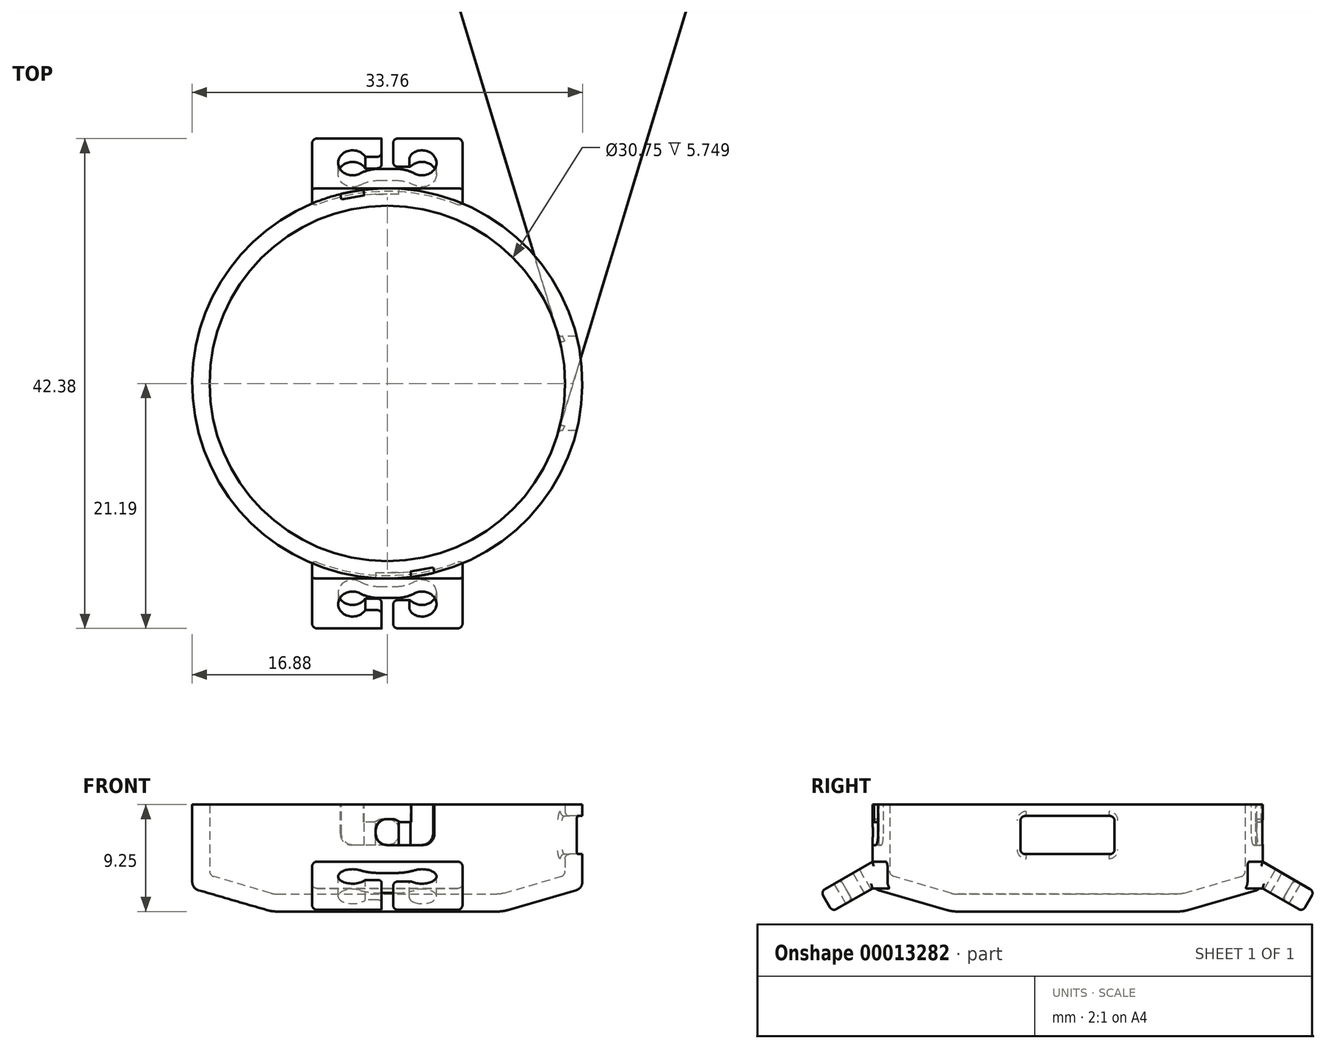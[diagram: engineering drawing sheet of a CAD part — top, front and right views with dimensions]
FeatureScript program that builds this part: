
annotation { "Feature Type Name" : "Feature", "Feature Type Description" : "" }
export const myFeature = defineFeature(function(context is Context, id is Id, definition is map)
    precondition{}
    {
        {
            var Q0;
            Q0=qCreatedBy(makeId("Front.planeOp"),FACE);
            var sketch = newSketch(context, id + "F0", { "sketchPlane" : qUnion([Q0])});
            skLineSegment(sketch, "E0", {"start": v(-16.88, 7.25) * mm, "end": v(-16.88, 0.56) * mm});
            skLineSegment(sketch, "E1", {"start": v(-16.33, -0.16) * mm, "end": v(-10.41, -1.88) * mm});
            skLineSegment(sketch, "E2", {"start": v(-9.57, -2) * mm, "end": v(0, -2) * mm});
            skLineSegment(sketch, "E3", {"start": v(0, -2) * mm, "end": v(0, -0.5) * mm});
            skLineSegment(sketch, "E4", {"start": v(0, -0.5) * mm, "end": v(-9.5, -0.5) * mm});
            skLineSegment(sketch, "E5", {"start": v(-10.06, -0.42) * mm, "end": v(-15.01, 1.02) * mm});
            skLineSegment(sketch, "E6", {"start": v(-15.38, 7.25) * mm, "end": v(-16.88, 7.25) * mm});
            skLineSegment(sketch, "E7", {"start": v(-15.38, 7.25) * mm, "end": v(-15.38, 1.5) * mm});
            skPoint(sketch, "E8.visualSharp", {"position": v(-16.88, 0) * mm});
            skArc(sketch, "E8.filletArc", {"start": v(-16.88, 0.56) * mm, "mid": v(-16.72, 0.11) * mm, "end": v(-16.33, -0.16) * mm});
            skPoint(sketch, "E9.visualSharp", {"position": v(-10, -2) * mm});
            skArc(sketch, "E9.filletArc", {"start": v(-10.41, -1.88) * mm, "mid": v(-10, -1.97) * mm, "end": v(-9.57, -2) * mm});
            skPoint(sketch, "E10.visualSharp", {"position": v(-15.38, 1.13) * mm});
            skArc(sketch, "E10.filletArc", {"start": v(-15.38, 1.5) * mm, "mid": v(-15.27, 1.2) * mm, "end": v(-15.01, 1.02) * mm});
            skPoint(sketch, "E11.visualSharp", {"position": v(-9.79, -0.5) * mm});
            skArc(sketch, "E11.filletArc", {"start": v(-10.06, -0.42) * mm, "mid": v(-9.78, -0.48) * mm, "end": v(-9.5, -0.5) * mm});
            skSolve(sketch);
        }
        {
            var Q0;
            Q0=makeQuery(id+"F0.imprint","IMPRINT",FACE,{"disambiguationData":[TD([[makeQuery(id+"F0.imprint","IMPRINT",EDGE,{"derivedFrom":sQuery(id+"F0.wireOp",EDGE,"E0")}),1.0]])]});
            var Q1;
            Q1=sQuery(id+"F0.wireOp",EDGE,"E3");
            revolve(context, id + "F1", {"entities" : qUnion([Q0]), "axis" : qUnion([Q1]), "revolveType" : RevolveType.FULL});
        }
        {
            var Q0;
            Q0=qCreatedBy(makeId("Right.planeOp"),FACE);
            var sketch = newSketch(context, id + "F2", { "sketchPlane" : qUnion([Q0])});
            skLineSegment(sketch, "E12", {"start": v(-15.38, 0) * mm, "end": v(-15.38, 2.3) * mm});
            skLineSegment(sketch, "E13", {"start": v(-15.38, 2.3) * mm, "end": v(-16.88, 2.3) * mm});
            skLineSegment(sketch, "E14", {"start": v(-16.88, 2.3) * mm, "end": v(-21.34, -0.27) * mm});
            skLineSegment(sketch, "E15", {"start": v(-21.34, -0.27) * mm, "end": v(-20.34, -2) * mm});
            skLineSegment(sketch, "E16", {"start": v(-20.34, -2) * mm, "end": v(-16.88, 0) * mm});
            skLineSegment(sketch, "E17", {"start": v(-16.88, 0) * mm, "end": v(-15.38, 0) * mm});
            skSolve(sketch);
        }
        {
            var Q0;
            Q0=makeQuery(id+"F2.imprint","IMPRINT",FACE,{"disambiguationData":[TD([[makeQuery(id+"F2.imprint","IMPRINT",EDGE,{"derivedFrom":sQuery(id+"F2.wireOp",EDGE,"E12")}),1.0]])]});
            extrude(context, id + "F3", {"entities" : qUnion([Q0]), "operationType" : NewBodyOperationType.ADD, "depth" : 6.5 * mm, "hasSecondDirection" : true, "secondDirectionOppositeDirection" : true, "secondDirectionDepth" : 6.5 * mm});
        }
        {
            var Q0;
            Q0=makeQuery(id+"F3.opExtrude","SWEPT_FACE",FACE,{"disambiguationData":[OSD([sQuery(id+"F2.wireOp",EDGE,"E14")])]});
            var sketch = newSketch(context, id + "F4", { "sketchPlane" : qUnion([Q0])});
            skLineSegment(sketch, "E18", {"start": v(-0.5, -18.61) * mm, "end": v(0.5, -18.61) * mm});
            skLineSegment(sketch, "E19", {"start": v(0.5, -18.61) * mm, "end": v(0.5, -16.61) * mm});
            skLineSegment(sketch, "E20", {"start": v(0.5, -16.61) * mm, "end": v(3, -16.61) * mm});
            skLineSegment(sketch, "E21", {"start": v(3, -16.61) * mm, "end": v(3, -15.41) * mm});
            skLineSegment(sketch, "E22", {"start": v(3, -15.41) * mm, "end": v(-3, -15.41) * mm});
            skLineSegment(sketch, "E23", {"start": v(-3, -15.41) * mm, "end": v(-3, -16.61) * mm});
            skLineSegment(sketch, "E24", {"start": v(-3, -16.61) * mm, "end": v(-0.5, -16.61) * mm});
            skLineSegment(sketch, "E25", {"start": v(-0.5, -16.61) * mm, "end": v(-0.5, -18.61) * mm});
            skCircle(sketch, "E26", {"center": v(-3, -16.01) * mm, "radius": 1.25 * mm});
            skCircle(sketch, "E27", {"center": v(3, -16.01) * mm, "radius": 1.25 * mm});
            skSolve(sketch);
        }
        {
            var Q0;
            {var subQ5=sQuery(id+"F4.wireOp",EDGE,"E23");Q0=makeQuery(id+"F4.imprint","IMPRINT",FACE,{"disambiguationData":[TD([[makeQuery(id+"F4.imprint","IMPRINT",EDGE,{"derivedFrom":subQ5}),-1.0]])]});}
            var Q1;
            {var subQ5=sQuery(id+"F4.wireOp",EDGE,"E23");Q1=makeQuery(id+"F4.imprint","IMPRINT",FACE,{"disambiguationData":[TD([[makeQuery(id+"F4.imprint","IMPRINT",EDGE,{"derivedFrom":subQ5}),1.0]])]});}
            var Q2;
            Q2=makeQuery(id+"F4.imprint","IMPRINT",FACE,{"disambiguationData":[TD([[makeQuery(id+"F4.imprint","IMPRINT",EDGE,{"derivedFrom":sQuery(id+"F4.wireOp",EDGE,"E18")}),-1.0]])]});
            var Q3;
            {var subQ5=sQuery(id+"F4.wireOp",EDGE,"E21");Q3=makeQuery(id+"F4.imprint","IMPRINT",FACE,{"disambiguationData":[TD([[makeQuery(id+"F4.imprint","IMPRINT",EDGE,{"derivedFrom":subQ5}),1.0]])]});}
            var Q4;
            {var subQ5=sQuery(id+"F4.wireOp",EDGE,"E21");Q4=makeQuery(id+"F4.imprint","IMPRINT",FACE,{"disambiguationData":[TD([[makeQuery(id+"F4.imprint","IMPRINT",EDGE,{"derivedFrom":subQ5}),-1.0]])]});}
            extrude(context, id + "F5", {"entities" : qUnion([Q0, Q1, Q2, Q3, Q4]), "operationType" : NewBodyOperationType.REMOVE, "endBound" : BoundingType.UP_TO_NEXT, "oppositeDirection" : true, "depth" : 25 * mm});
        }
        {
            var Q0;
            Q0=makeQuery(id+"F5.boolean.opBoolean","COPY",EDGE,{"derivedFrom":makeQuery(id+"F5.opExtrude","SWEPT_EDGE",EDGE,{"disambiguationData":[OSD([sQuery(id+"F4.wireOp",EDGE,"E22"),sQuery(id+"F4.wireOp",EDGE,"E26")])]})});
            var Q1;
            Q1=makeQuery(id+"F5.boolean.opBoolean","COPY",EDGE,{"derivedFrom":makeQuery(id+"F5.opExtrude","SWEPT_EDGE",EDGE,{"disambiguationData":[OSD([sQuery(id+"F4.wireOp",EDGE,"E22"),sQuery(id+"F4.wireOp",EDGE,"E27")])]})});
            fillet(context, id + "F6", {"entities" : qUnion([Q0, Q1]), "radius" : 3 * mm, "tangentPropagation" : true, "allowEdgeOverflow" : false});
        }
        {
            var Q0;
            Q0=makeQuery(id+"F5.boolean.opBoolean","COPY",EDGE,{"derivedFrom":makeQuery(id+"F5.opExtrude","SWEPT_EDGE",EDGE,{"disambiguationData":[OSD([sQuery(id+"F2.wireOp",EDGE,"E14"),sQuery(id+"F2.wireOp",EDGE,"E15"),sQuery(id+"F4.wireOp",EDGE,"E18"),sQuery(id+"F4.wireOp",EDGE,"E25")])]})});
            var Q1;
            Q1=makeQuery(id+"F5.boolean.opBoolean","COPY",EDGE,{"derivedFrom":makeQuery(id+"F5.opExtrude","SWEPT_EDGE",EDGE,{"disambiguationData":[OSD([sQuery(id+"F2.wireOp",EDGE,"E14"),sQuery(id+"F2.wireOp",EDGE,"E15"),sQuery(id+"F4.wireOp",EDGE,"E18"),sQuery(id+"F4.wireOp",EDGE,"E19")])]})});
            var Q2;
            Q2=makeQuery(id+"F5.boolean.opBoolean","COPY",EDGE,{"derivedFrom":makeQuery(id+"F5.opExtrude","SWEPT_EDGE",EDGE,{"disambiguationData":[OSD([sQuery(id+"F4.wireOp",EDGE,"E24"),sQuery(id+"F4.wireOp",EDGE,"E25")])]})});
            var Q3;
            Q3=makeQuery(id+"F5.boolean.opBoolean","COPY",EDGE,{"derivedFrom":makeQuery(id+"F5.opExtrude","SWEPT_EDGE",EDGE,{"disambiguationData":[OSD([sQuery(id+"F4.wireOp",EDGE,"E19"),sQuery(id+"F4.wireOp",EDGE,"E20")])]})});
            fillet(context, id + "F7", {"entities" : qUnion([Q0, Q1, Q2, Q3]), "radius" : .4 * mm, "tangentPropagation" : true, "allowEdgeOverflow" : false});
        }
        {
            var Q0;
            Q0=makeQuery(id+"F3.opExtrude","CAP_EDGE",EDGE,{"disambiguationData":[OSD([sQuery(id+"F2.wireOp",EDGE,"E13")])],"isStart":true});
            var Q1;
            Q1=makeQuery(id+"F3.opExtrude","CAP_EDGE",EDGE,{"disambiguationData":[OSD([sQuery(id+"F2.wireOp",EDGE,"E14")])],"isStart":true});
            var Q2;
            {var subQ0=sQuery(id+"F2.wireOp",EDGE,"E15");var subQ1=sQuery(id+"F2.wireOp",EDGE,"E14");Q2=makeQuery(id+"F5.boolean.opBoolean","SPLIT",EDGE,{"disambiguationData":[TD([makeQuery(id+"F5.opExtrude","SWEPT_FACE",FACE,{"disambiguationData":[OSD([sQuery(id+"F4.wireOp",EDGE,"E25")])]})])],"derivedFrom":makeQuery(id+"F3.opExtrude","SWEPT_EDGE",EDGE,{"disambiguationData":[OSD([subQ1,subQ0])]})});}
            var Q3;
            Q3=makeQuery(id+"F5.boolean.opBoolean","COPY",EDGE,{"derivedFrom":makeQuery(id+"F5.opExtrude","CAP_EDGE",EDGE,{"disambiguationData":[OSD([sQuery(id+"F4.wireOp",EDGE,"E26")])],"isStart":true})});
            var Q4;
            Q4=makeQuery(id+"F3.opExtrude","CAP_EDGE",EDGE,{"disambiguationData":[OSD([sQuery(id+"F2.wireOp",EDGE,"E13")])],"isStart":false});
            var Q5;
            Q5=makeQuery(id+"F3.opExtrude","CAP_EDGE",EDGE,{"disambiguationData":[OSD([sQuery(id+"F2.wireOp",EDGE,"E14")])],"isStart":false});
            var Q6;
            {var subQ0=sQuery(id+"F2.wireOp",EDGE,"E15");var subQ1=sQuery(id+"F2.wireOp",EDGE,"E14");Q6=makeQuery(id+"F5.boolean.opBoolean","SPLIT",EDGE,{"disambiguationData":[TD([makeQuery(id+"F5.opExtrude","SWEPT_FACE",FACE,{"disambiguationData":[OSD([sQuery(id+"F4.wireOp",EDGE,"E19")])]})])],"derivedFrom":makeQuery(id+"F3.opExtrude","SWEPT_EDGE",EDGE,{"disambiguationData":[OSD([subQ1,subQ0])]})});}
            var Q7;
            Q7=makeQuery(id+"F3.opExtrude","CAP_EDGE",EDGE,{"disambiguationData":[OSD([sQuery(id+"F2.wireOp",EDGE,"E17")])],"isStart":false});
            var Q8;
            Q8=makeQuery(id+"F3.opExtrude","CAP_EDGE",EDGE,{"disambiguationData":[OSD([sQuery(id+"F2.wireOp",EDGE,"E16")])],"isStart":false});
            var Q9;
            {var subQ0=sQuery(id+"F2.wireOp",EDGE,"E16");var subQ1=sQuery(id+"F2.wireOp",EDGE,"E15");Q9=makeQuery(id+"F5.boolean.opBoolean","SPLIT",EDGE,{"disambiguationData":[TD([makeQuery(id+"F5.opExtrude","SWEPT_FACE",FACE,{"disambiguationData":[OSD([sQuery(id+"F4.wireOp",EDGE,"E19")])]})])],"derivedFrom":makeQuery(id+"F3.opExtrude","SWEPT_EDGE",EDGE,{"disambiguationData":[OSD([subQ1,subQ0])]})});}
            var Q10;
            Q10=makeQuery(id+"F5.boolean.opBoolean","COPY",EDGE,{"derivedFrom":makeQuery(id+"F5.opExtrude","CAP_EDGE",EDGE,{"disambiguationData":[OSD([sQuery(id+"F4.wireOp",EDGE,"E27")])],"isStart":false})});
            var Q11;
            Q11=makeQuery(id+"F3.opExtrude","CAP_EDGE",EDGE,{"disambiguationData":[OSD([sQuery(id+"F2.wireOp",EDGE,"E17")])],"isStart":true});
            var Q12;
            Q12=makeQuery(id+"F3.opExtrude","CAP_EDGE",EDGE,{"disambiguationData":[OSD([sQuery(id+"F2.wireOp",EDGE,"E16")])],"isStart":true});
            var Q13;
            {var subQ0=sQuery(id+"F2.wireOp",EDGE,"E16");var subQ1=sQuery(id+"F2.wireOp",EDGE,"E15");Q13=makeQuery(id+"F5.boolean.opBoolean","SPLIT",EDGE,{"disambiguationData":[TD([makeQuery(id+"F5.opExtrude","SWEPT_FACE",FACE,{"disambiguationData":[OSD([sQuery(id+"F4.wireOp",EDGE,"E25")])]})])],"derivedFrom":makeQuery(id+"F3.opExtrude","SWEPT_EDGE",EDGE,{"disambiguationData":[OSD([subQ1,subQ0])]})});}
            var Q14;
            Q14=makeQuery(id+"F3.opExtrude","CAP_EDGE",EDGE,{"disambiguationData":[OSD([sQuery(id+"F2.wireOp",EDGE,"E15")])],"isStart":true});
            var Q15;
            Q15=makeQuery(id+"F3.opExtrude","CAP_EDGE",EDGE,{"disambiguationData":[OSD([sQuery(id+"F2.wireOp",EDGE,"E15")])],"isStart":false});
            fillet(context, id + "F8", {"entities" : qUnion([Q0, Q1, Q2, Q3, Q4, Q5, Q6, Q7, Q8, Q9, Q10, Q11, Q12, Q13, Q14, Q15]), "radius" : .4 * mm, "tangentPropagation" : true, "allowEdgeOverflow" : false});
        }
        {
            var Q0;
            Q0=makeQuery(id+"F1.opRevolve","SWEPT_BODY",BODY,{"disambiguationData":[OSD([sQuery(id+"F0.wireOp",EDGE,"E0"),sQuery(id+"F0.wireOp",EDGE,"E1"),sQuery(id+"F0.wireOp",EDGE,"E2"),sQuery(id+"F0.wireOp",EDGE,"E3"),sQuery(id+"F0.wireOp",EDGE,"E4"),sQuery(id+"F0.wireOp",EDGE,"E5"),sQuery(id+"F0.wireOp",EDGE,"E6"),sQuery(id+"F0.wireOp",EDGE,"E7"),sQuery(id+"F0.wireOp",EDGE,"E8.filletArc"),sQuery(id+"F0.wireOp",EDGE,"E9.filletArc"),sQuery(id+"F0.wireOp",EDGE,"E10.filletArc"),sQuery(id+"F0.wireOp",EDGE,"E11.filletArc")])]});
            var Q1;
            Q1=qCreatedBy(makeId("Front.planeOp"),FACE);
            mirror(context, id + "F9", {"operationType" : NewBodyOperationType.ADD, "entities" : qUnion([Q0]), "mirrorPlane" : qUnion([Q1])});
        }
        {
            var Q0;
            Q0=qCreatedBy(makeId("Right.planeOp"),FACE);
            var sketch = newSketch(context, id + "F10", { "sketchPlane" : qUnion([Q0])});
            skLineSegment(sketch, "E28.bottom", {"start": v(-3.68, 6.26) * mm, "end": v(3.68, 6.26) * mm});
            skLineSegment(sketch, "E28.top", {"start": v(-3.68, 2.96) * mm, "end": v(3.68, 2.96) * mm});
            skLineSegment(sketch, "E28.left", {"start": v(-4.08, 5.86) * mm, "end": v(-4.08, 3.36) * mm});
            skLineSegment(sketch, "E28.right", {"start": v(4.08, 5.86) * mm, "end": v(4.08, 3.36) * mm});
            skPoint(sketch, "E29.visualSharp", {"position": v(-4.08, 6.26) * mm});
            skArc(sketch, "E29.filletArc", {"start": v(-3.68, 6.26) * mm, "mid": v(-3.96, 6.14) * mm, "end": v(-4.08, 5.86) * mm});
            skPoint(sketch, "E30.visualSharp", {"position": v(4.08, 6.26) * mm});
            skArc(sketch, "E30.filletArc", {"start": v(4.08, 5.86) * mm, "mid": v(3.96, 6.14) * mm, "end": v(3.68, 6.26) * mm});
            skPoint(sketch, "E31.visualSharp", {"position": v(4.08, 2.96) * mm});
            skArc(sketch, "E31.filletArc", {"start": v(3.68, 2.96) * mm, "mid": v(3.96, 3.08) * mm, "end": v(4.08, 3.36) * mm});
            skPoint(sketch, "E32.visualSharp", {"position": v(-4.08, 2.96) * mm});
            skArc(sketch, "E32.filletArc", {"start": v(-4.08, 3.36) * mm, "mid": v(-3.96, 3.08) * mm, "end": v(-3.68, 2.96) * mm});
            skSolve(sketch);
        }
        {
            var Q0;
            Q0=qSketchRegion(id+"F10",true);
            var Q1;
            Q1=makeQuery(id+"F1.opRevolve","SWEPT_FACE",FACE,{"disambiguationData":[OSD([sQuery(id+"F0.wireOp",EDGE,"E0")])]});
            extrude(context, id + "F11", {"entities" : qUnion([Q0]), "operationType" : NewBodyOperationType.REMOVE, "endBound" : BoundingType.UP_TO_SURFACE, "endBoundEntityFace" : qUnion([Q1]), "depth" : 25 * mm});
        }
        {
            var Q0;
            Q0=makeQuery(id+"F11.boolean.opBoolean","COPY",EDGE,{"derivedFrom":makeQuery(id+"F11.opExtrude","CAP_EDGE",EDGE,{"disambiguationData":[OSD([sQuery(id+"F10.wireOp",EDGE,"E28.bottom")])],"isStart":false})});
            var Q1;
            Q1=makeQuery(id+"F11.boolean.opBoolean","INTERSECT",EDGE,{"derivedFrom":[makeQuery(id+"F1.opRevolve","SWEPT_FACE",FACE,{"disambiguationData":[OSD([sQuery(id+"F0.wireOp",EDGE,"E7")])]}),makeQuery(id+"F11.opExtrude","SWEPT_FACE",FACE,{"disambiguationData":[OSD([sQuery(id+"F10.wireOp",EDGE,"E28.top")])]})]});
            fillet(context, id + "F12", {"entities" : qUnion([Q0, Q1]), "radius" : .4 * mm, "tangentPropagation" : true, "allowEdgeOverflow" : false});
        }
        {
            var Q0;
            Q0=makeQuery(id+"F1.opRevolve","SWEPT_FACE",FACE,{"disambiguationData":[OSD([sQuery(id+"F0.wireOp",EDGE,"E6")])]});
            cPlane(context, id + "F13", {"entities" : qUnion([Q0]), "cplaneType" : CPlaneType.OFFSET, "offset" : 1.5 * mm, "oppositeDirection" : true, "width" : 150 * mm, "height" : 150 * mm});
        }
        {
            var Q0;
            Q0=qCreatedBy(id+"F13.planeOp",FACE);
            var sketch = newSketch(context, id + "F14", { "sketchPlane" : qUnion([Q0])});
            skLineSegment(sketch, "E33", {"start": v(0, 0) * mm, "end": v(0, -16.88) * mm, "construction": true});
            skCircle(sketch, "E34", {"center": v(0, 0) * mm, "radius": 16.88 * mm});
            skLineSegment(sketch, "E35", {"start": v(-1, -16.38) * mm, "end": v(1, -16.38) * mm});
            skLineSegment(sketch, "E36", {"start": v(0, 0) * mm, "end": v(-1.03, -16.84) * mm});
            skLineSegment(sketch, "E37", {"start": v(0, 0) * mm, "end": v(1.03, -16.84) * mm});
            skLineSegment(sketch, "E38", {"start": v(1, -16.38) * mm, "end": v(2, -16.28) * mm});
            skLineSegment(sketch, "E39", {"start": v(0, 0) * mm, "end": v(2.05, -16.75) * mm});
            skLineSegment(sketch, "E40", {"start": v(0, 0) * mm, "end": v(1.5, -16.33) * mm, "construction": true});
            skLineSegment(sketch, "E41", {"start": v(2, -16.28) * mm, "end": v(3.96, -15.92) * mm});
            skLineSegment(sketch, "E42", {"start": v(0, 0) * mm, "end": v(4.08, -16.38) * mm});
            skLineSegment(sketch, "E43", {"start": v(0, 0) * mm, "end": v(2.98, -16.1) * mm, "construction": true});
            skLineSegment(sketch, "E44.1.0", {"start": v(0, 0) * mm, "end": v(-4.08, 16.38) * mm});
            skLineSegment(sketch, "E44.1.1", {"start": v(-2, 16.28) * mm, "end": v(-3.96, 15.92) * mm});
            skLineSegment(sketch, "E44.1.2", {"start": v(0, 0) * mm, "end": v(-2.05, 16.75) * mm});
            skLineSegment(sketch, "E44.1.3", {"start": v(-1, 16.38) * mm, "end": v(-2, 16.28) * mm});
            skLineSegment(sketch, "E44.1.4", {"start": v(0, 0) * mm, "end": v(-1.03, 16.84) * mm});
            skLineSegment(sketch, "E44.1.5", {"start": v(1, 16.38) * mm, "end": v(-1, 16.38) * mm});
            skLineSegment(sketch, "E44.1.6", {"start": v(0, 0) * mm, "end": v(1.03, 16.84) * mm});
            skLineSegment(sketch, "E44.anchor1", {"start": v(0, 0) * mm, "end": v(4.08, -16.38) * mm, "construction": true});
            skLineSegment(sketch, "E44.anchor2", {"start": v(0, 0) * mm, "end": v(-4.08, 16.38) * mm, "construction": true});
            skSolve(sketch);
        }
        {
            var Q0;
            {var subQ3=sQuery(id+"F14.wireOp",EDGE,"E35");Q0=makeQuery(id+"F14.imprint","IMPRINT",FACE,{"disambiguationData":[TD([[makeQuery(id+"F14.imprint","IMPRINT",EDGE,{"derivedFrom":subQ3}),-1.0]])]});}
            var Q1;
            {var subQ3=sQuery(id+"F14.wireOp",EDGE,"E44.1.5");Q1=makeQuery(id+"F14.imprint","IMPRINT",FACE,{"disambiguationData":[TD([[makeQuery(id+"F14.imprint","IMPRINT",EDGE,{"derivedFrom":subQ3}),-1.0]])]});}
            extrude(context, id + "F15", {"entities" : qUnion([Q0, Q1]), "operationType" : NewBodyOperationType.REMOVE, "oppositeDirection" : true, "depth" : 2 * mm, "hasSecondDirection" : true, "secondDirectionOppositeDirection" : false, "secondDirectionDepth" : .25 * mm});
        }
        {
            var Q0;
            {var subQ3=sQuery(id+"F14.wireOp",EDGE,"E38");Q0=makeQuery(id+"F14.imprint","IMPRINT",FACE,{"disambiguationData":[TD([[makeQuery(id+"F14.imprint","IMPRINT",EDGE,{"derivedFrom":subQ3}),-1.0]])]});}
            var Q1;
            {var subQ3=sQuery(id+"F14.wireOp",EDGE,"E44.1.3");Q1=makeQuery(id+"F14.imprint","IMPRINT",FACE,{"disambiguationData":[TD([[makeQuery(id+"F14.imprint","IMPRINT",EDGE,{"derivedFrom":subQ3}),-1.0]])]});}
            extrude(context, id + "F16", {"entities" : qUnion([Q0, Q1]), "operationType" : NewBodyOperationType.REMOVE, "oppositeDirection" : true, "depth" : 2 * mm});
        }
        {
            var Q0;
            {var subQ3=sQuery(id+"F14.wireOp",EDGE,"E41");Q0=makeQuery(id+"F14.imprint","IMPRINT",FACE,{"disambiguationData":[TD([[makeQuery(id+"F14.imprint","IMPRINT",EDGE,{"derivedFrom":subQ3}),-1.0]])]});}
            var Q1;
            {var subQ3=sQuery(id+"F14.wireOp",EDGE,"E44.1.1");Q1=makeQuery(id+"F14.imprint","IMPRINT",FACE,{"disambiguationData":[TD([[makeQuery(id+"F14.imprint","IMPRINT",EDGE,{"derivedFrom":subQ3}),-1.0]])]});}
            extrude(context, id + "F17", {"entities" : qUnion([Q0, Q1]), "operationType" : NewBodyOperationType.REMOVE, "oppositeDirection" : true, "depth" : 2 * mm, "hasSecondDirection" : true, "secondDirectionBound" : SecondDirectionBoundingType.UP_TO_NEXT, "secondDirectionOppositeDirection" : false, "secondDirectionDepth" : 25 * mm});
        }
        {
            var Q0;
            Q0=makeQuery(id+"F15.boolean.opBoolean","COPY",EDGE,{"derivedFrom":makeQuery(id+"F15.opExtrude","CAP_EDGE",EDGE,{"disambiguationData":[OSD([sQuery(id+"F14.wireOp",EDGE,"E37")])],"isStart":true})});
            var Q1;
            Q1=makeQuery(id+"F15.boolean.opBoolean","COPY",EDGE,{"derivedFrom":makeQuery(id+"F15.opExtrude","CAP_EDGE",EDGE,{"disambiguationData":[OSD([sQuery(id+"F14.wireOp",EDGE,"E36")])],"isStart":true})});
            var Q2;
            Q2=makeQuery(id+"F15.boolean.opBoolean","COPY",EDGE,{"derivedFrom":makeQuery(id+"F15.opExtrude","CAP_EDGE",EDGE,{"disambiguationData":[OSD([sQuery(id+"F14.wireOp",EDGE,"E36")])],"isStart":false})});
            var Q3;
            Q3=makeQuery(id+"F17.boolean.opBoolean","COPY",EDGE,{"derivedFrom":makeQuery(id+"F17.opExtrude","CAP_EDGE",EDGE,{"disambiguationData":[OSD([sQuery(id+"F14.wireOp",EDGE,"E42")])],"isStart":false})});
            var Q4;
            Q4=makeQuery(id+"F15.boolean.opBoolean","COPY",EDGE,{"derivedFrom":makeQuery(id+"F15.opExtrude","CAP_EDGE",EDGE,{"disambiguationData":[OSD([sQuery(id+"F14.wireOp",EDGE,"E44.1.4")])],"isStart":true})});
            var Q5;
            Q5=makeQuery(id+"F15.boolean.opBoolean","COPY",EDGE,{"derivedFrom":makeQuery(id+"F15.opExtrude","CAP_EDGE",EDGE,{"disambiguationData":[OSD([sQuery(id+"F14.wireOp",EDGE,"E44.1.6")])],"isStart":true})});
            var Q6;
            Q6=makeQuery(id+"F15.boolean.opBoolean","COPY",EDGE,{"derivedFrom":makeQuery(id+"F15.opExtrude","CAP_EDGE",EDGE,{"disambiguationData":[OSD([sQuery(id+"F14.wireOp",EDGE,"E44.1.6")])],"isStart":false})});
            var Q7;
            Q7=makeQuery(id+"F17.boolean.opBoolean","COPY",EDGE,{"derivedFrom":makeQuery(id+"F17.opExtrude","CAP_EDGE",EDGE,{"disambiguationData":[OSD([sQuery(id+"F14.wireOp",EDGE,"E44.1.0")])],"isStart":false})});
            fillet(context, id + "F18", {"entities" : qUnion([Q0, Q1, Q2, Q3, Q4, Q5, Q6, Q7]), "radius" : 1 * mm, "tangentPropagation" : true, "allowEdgeOverflow" : false});
        }
        {
            var Q0;
            Q0=makeQuery(id+"F16.boolean.opBoolean","COPY",EDGE,{"derivedFrom":makeQuery(id+"F16.opExtrude","CAP_EDGE",EDGE,{"disambiguationData":[OSD([sQuery(id+"F14.wireOp",EDGE,"E37")])],"isStart":true})});
            var Q1;
            Q1=makeQuery(id+"F16.boolean.opBoolean","COPY",EDGE,{"derivedFrom":makeQuery(id+"F16.opExtrude","CAP_EDGE",EDGE,{"disambiguationData":[OSD([sQuery(id+"F14.wireOp",EDGE,"E39")])],"isStart":true})});
            var Q2;
            Q2=makeQuery(id+"F16.boolean.opBoolean","COPY",EDGE,{"derivedFrom":makeQuery(id+"F16.opExtrude","CAP_EDGE",EDGE,{"disambiguationData":[OSD([sQuery(id+"F14.wireOp",EDGE,"E44.1.2")])],"isStart":true})});
            var Q3;
            Q3=makeQuery(id+"F16.boolean.opBoolean","COPY",EDGE,{"derivedFrom":makeQuery(id+"F16.opExtrude","CAP_EDGE",EDGE,{"disambiguationData":[OSD([sQuery(id+"F14.wireOp",EDGE,"E44.1.4")])],"isStart":true})});
            var Q4;
            {var subQ0=sQuery(id+"F14.wireOp",EDGE,"E37");Q4=makeQuery(id+"F18.opFillet","BLEND_EDGE",EDGE,{"blendedFrom":[makeQuery(id+"F15.boolean.opBoolean","COPY",EDGE,{"derivedFrom":makeQuery(id+"F15.opExtrude","CAP_EDGE",EDGE,{"disambiguationData":[OSD([subQ0])],"isStart":true})}),makeQuery(id+"F16.boolean.opBoolean","COPY",FACE,{"derivedFrom":makeQuery(id+"F16.opExtrude","CAP_FACE",FACE,{"disambiguationData":[OSD([sQuery(id+"F14.wireOp",EDGE,"E34"),subQ0,sQuery(id+"F14.wireOp",EDGE,"E38"),sQuery(id+"F14.wireOp",EDGE,"E39")])],"isStart":true})})],"blendedInto":[makeQuery(id+"F16.boolean.opBoolean","COPY",FACE,{"derivedFrom":makeQuery(id+"F16.opExtrude","CAP_FACE",FACE,{"disambiguationData":[OSD([sQuery(id+"F14.wireOp",EDGE,"E34"),subQ0,sQuery(id+"F14.wireOp",EDGE,"E38"),sQuery(id+"F14.wireOp",EDGE,"E39")])],"isStart":true})})]});}
            var Q5;
            {var subQ0=sQuery(id+"F14.wireOp",EDGE,"E44.1.4");Q5=makeQuery(id+"F18.opFillet","BLEND_EDGE",EDGE,{"blendedFrom":[makeQuery(id+"F15.boolean.opBoolean","COPY",EDGE,{"derivedFrom":makeQuery(id+"F15.opExtrude","CAP_EDGE",EDGE,{"disambiguationData":[OSD([subQ0])],"isStart":true})}),makeQuery(id+"F16.boolean.opBoolean","COPY",FACE,{"derivedFrom":makeQuery(id+"F16.opExtrude","CAP_FACE",FACE,{"disambiguationData":[OSD([sQuery(id+"F14.wireOp",EDGE,"E34"),sQuery(id+"F14.wireOp",EDGE,"E44.1.2"),sQuery(id+"F14.wireOp",EDGE,"E44.1.3"),subQ0])],"isStart":true})})],"blendedInto":[makeQuery(id+"F16.boolean.opBoolean","COPY",FACE,{"derivedFrom":makeQuery(id+"F16.opExtrude","CAP_FACE",FACE,{"disambiguationData":[OSD([sQuery(id+"F14.wireOp",EDGE,"E34"),sQuery(id+"F14.wireOp",EDGE,"E44.1.2"),sQuery(id+"F14.wireOp",EDGE,"E44.1.3"),subQ0])],"isStart":true})})]});}
            fillet(context, id + "F19", {"entities" : qUnion([Q0, Q1, Q2, Q3, Q4, Q5]), "radius" : .25 * mm, "tangentPropagation" : true, "allowEdgeOverflow" : false});
        }
    });
